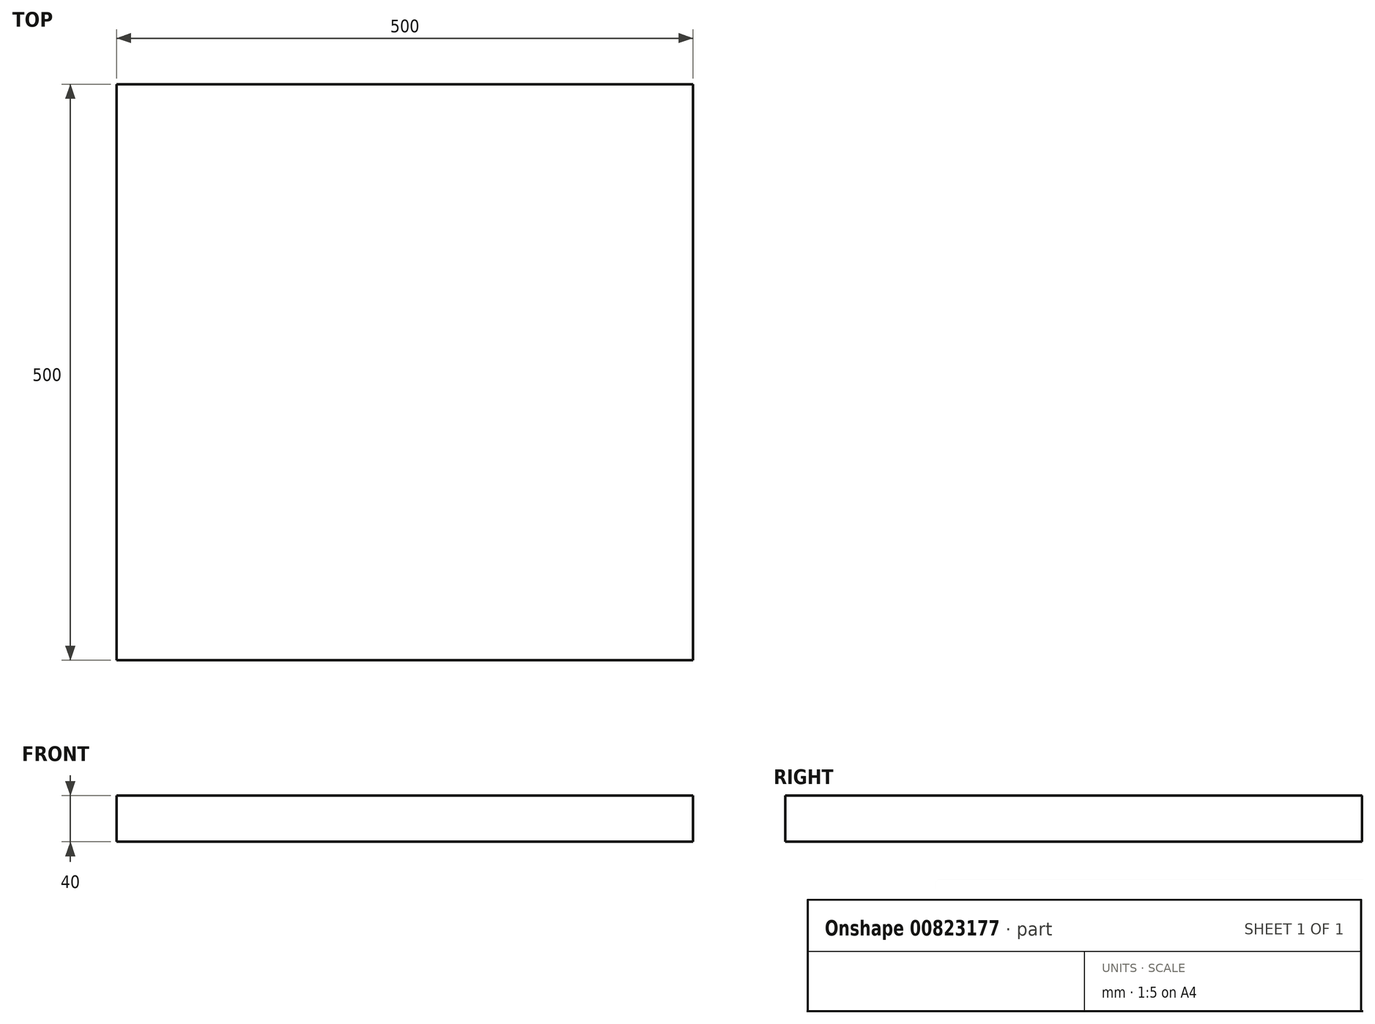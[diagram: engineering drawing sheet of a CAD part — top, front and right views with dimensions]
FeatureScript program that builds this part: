
annotation { "Feature Type Name" : "Feature", "Feature Type Description" : "" }
export const myFeature = defineFeature(function(context is Context, id is Id, definition is map)
    precondition{}
    {
        {
            var Q0;
            Q0=qCreatedBy(makeId("Top.planeOp"),FACE);
            var sketch = newSketch(context, id + "F0", { "sketchPlane" : qUnion([Q0])});
            skLineSegment(sketch, "E0.bottom", {"start": v(-362.02, 435.12) * mm, "end": v(137.98, 435.12) * mm});
            skLineSegment(sketch, "E0.top", {"start": v(-362.02, -64.88) * mm, "end": v(137.98, -64.88) * mm});
            skLineSegment(sketch, "E0.left", {"start": v(-362.02, 435.12) * mm, "end": v(-362.02, -64.88) * mm});
            skLineSegment(sketch, "E0.right", {"start": v(137.98, 435.12) * mm, "end": v(137.98, -64.88) * mm});
            skSolve(sketch);
        }
        {
            var Q0;
            Q0 = qSketchRegion(id + "F0", true);
            extrude(context, id + "F1", {"entities" : qUnion([Q0]), "depth" : 40 * mm, "offsetDistance" : 25 * mm});
        }
    });
